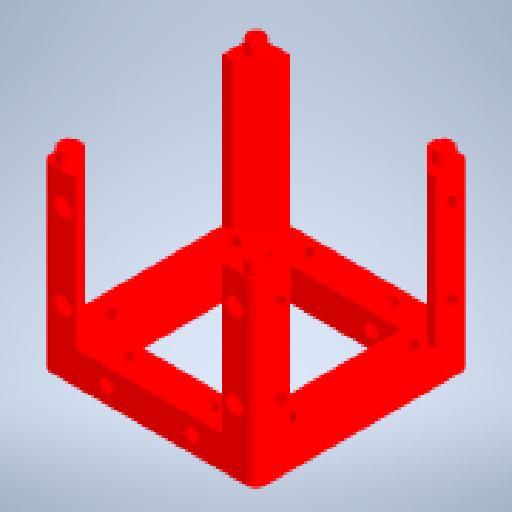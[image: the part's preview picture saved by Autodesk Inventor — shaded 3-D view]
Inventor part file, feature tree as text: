
AUTODESK INVENTOR PART (.ipt)
format: ipt  version: 2023.1 (Build 271208000, 208)  size: 346,624 bytes
history: native  units: mm
features: extrude x7, chamfer x7, sketch x3, pattern_linear x1, pattern_circular x1, fillet x1, projected_geometry x1
ambient origin geometry x8: Origin, YZ Plane, XZ Plane, XY Plane, X Axis, Y Axis, Z Axis, Center Point
bodies: Solid1 (feature_tree)
feature tree (21):
  sketch  "Sketch1"  dims[d0=49.8mm d1=49.8mm]
  extrude  "Extrusion1"  Depth=49.8mm
  extrude  "Extrusion2"  Depth=10.5mm
  extrude  "Extrusion3"  Depth=2.0mm
  extrude  "Extrusion4"  Depth=2.0mm
  chamfer  "Chamfer1"  Distance=3.0mm
  chamfer  "Chamfer2"  Distance=3.0mm
  chamfer  "Chamfer3"  Distance=4.2625mm
  chamfer  "Chamfer4"  Distance=0.675mm
  chamfer  "Chamfer5"  Distance=7.85mm
  chamfer  "Chamfer6"  Distance=7.85mm
  sketch  "Sketch2"  dims[d2=8.0mm d3=10.5mm]
  extrude  "Extrusion5"  Depth=2.0mm
  extrude  "Extrusion6"  Depth=2.0mm
  pattern_linear  "Rectangular Pattern1"  Count1=4 Spacing1=360.0deg
  pattern_circular  "Circular Pattern1"  [2 undecoded]
  extrude  "Extrusion7"  Depth=34.4mm TaperAngle=0.0deg
  fillet  "Fillet1"  Radius=0.375mm
  chamfer  "Chamfer7"  Distance=3.25mm
  sketch  "Sketch3"  dims[d4=10.5mm d5=4.1mm d6=4.15mm d7=3.0mm d8=3.0mm d9=4.2625mm d10=0.675mm d11=7.85mm d12=7.85mm d13=5.5mm d14=5.5mm d15=40.0mm d17=360.0deg d19=7.7mm d20=0.0mm d21=34.4mm d22=0.0mm d23=0.375mm d24=0.0mm d25=3.25mm d26=0.0mm d27=0.5mm d28=2.0mm d29=45.0deg d30=0.375mm d31=2.0mm d32=45.0deg d33=2.75mm d34=2.0mm d35=0.436332mm d36=2.75mm d37=2.0mm d38=0.436332mm d39=2.75mm d40=2.0mm d41=0.436332mm d42=2.75mm d43=2.0mm d44=0.436332mm d45=10.0mm d46=3.125mm d47=5.0mm d48=15.0mm d49=4.125mm d50=3.25mm d51=0.0mm d52=2.5mm d53=0.0mm d54=20.0mm d56=19.8mm d57=40.0mm d58=360.0deg d60=3.75mm d61=5.0mm d62=5.0mm d63=5.4125mm d64=0.0mm d65=2.0mm d66=0.025mm d67=2.0mm d68=0.436332mm]
  projected_geometry  "Projected Loop1"
note: 2 required parameter values undecoded (feature->parameter linkage not recoverable at this tier; creation-order binding heuristic only, values carry confidence <= 0.55)
